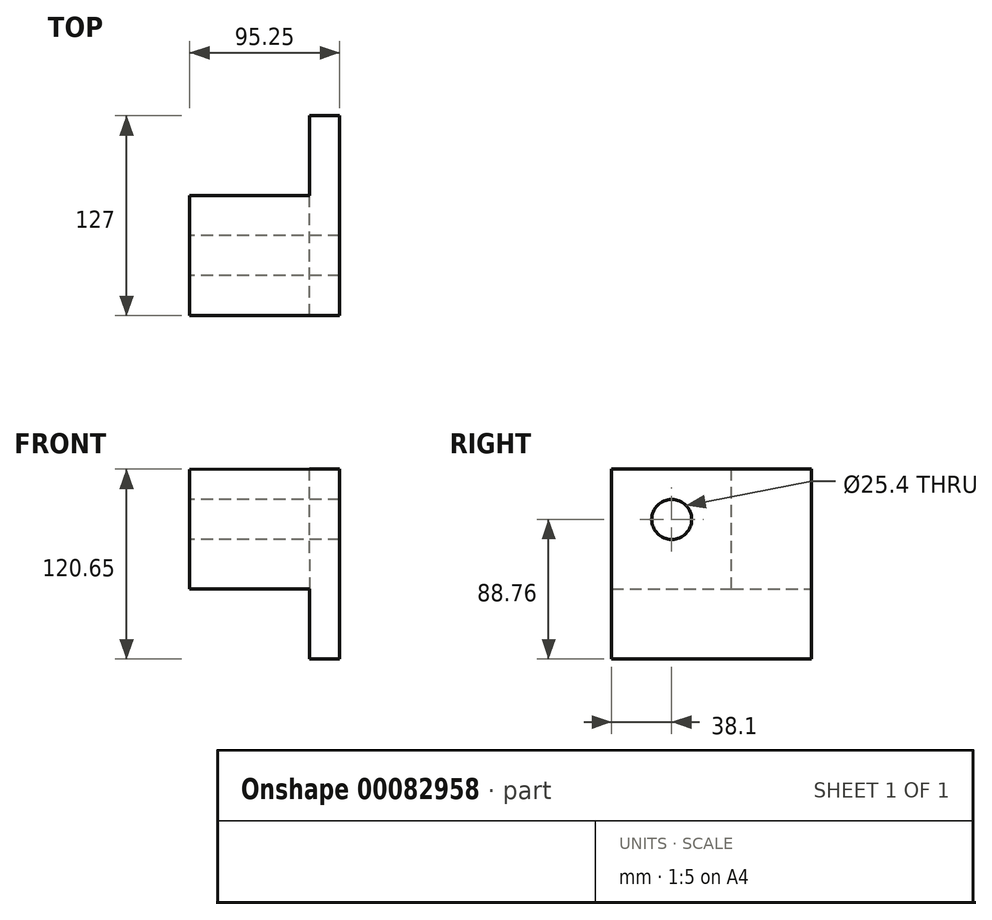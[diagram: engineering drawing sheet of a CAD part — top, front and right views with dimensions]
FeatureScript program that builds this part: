
annotation { "Feature Type Name" : "Feature", "Feature Type Description" : "" }
export const myFeature = defineFeature(function(context is Context, id is Id, definition is map)
    precondition{}
    {
        {
            var Q0;
            Q0=qCreatedBy(makeId("Front.planeOp"),FACE);
            var sketch = newSketch(context, id + "F0", { "sketchPlane" : qUnion([Q0])});
            skArc(sketch, "E0", {"start": v(0, 120.65) * mm, "mid": v(85.31, 85.31) * mm, "end": v(120.65, 0) * mm});
            skLineSegment(sketch, "E1", {"start": v(0, 120.65) * mm, "end": v(0, 0) * mm});
            skLineSegment(sketch, "E2", {"start": v(0, 0) * mm, "end": v(120.65, 0) * mm});
            skLineSegment(sketch, "E3.bottom", {"start": v(0, 120.65) * mm, "end": v(-19.05, 120.65) * mm});
            skLineSegment(sketch, "E3.top", {"start": v(0, 0) * mm, "end": v(-19.05, 0) * mm});
            skLineSegment(sketch, "E4", {"start": v(120.65, 0) * mm, "end": v(-95.25, 0) * mm});
            skLineSegment(sketch, "E5", {"start": v(-95.25, 0) * mm, "end": v(-95.25, 120.51) * mm});
            skLineSegment(sketch, "E6", {"start": v(-95.25, 120.51) * mm, "end": v(-19.05, 120.65) * mm});
            skSolve(sketch);
        }
        {
            var Q0;
            Q0=makeQuery(id+"F0.imprint","IMPRINT",FACE,{"disambiguationData":[TD([[makeQuery(id+"F0.imprint","IMPRINT",EDGE,{"derivedFrom":sQuery(id+"F0.wireOp",EDGE,"E3.bottom")}),1.0]])]});
            var Q1;
            {var subQ0=sQuery(id+"F0.wireOp",EDGE,"E0");Q1=makeQuery(id+"F0.imprint","IMPRINT",FACE,{"disambiguationData":[TD([[makeQuery(id+"F0.imprint","IMPRINT",EDGE,{"derivedFrom":subQ0}),-1.0]])]});}
            extrude(context, id + "F1", {"entities" : qUnion([Q0, Q1]), "depth" : 127 * mm});
        }
        {
            var Q0;
            Q0=makeQuery(id+"F1.opExtrude","SWEPT_FACE",FACE,{"disambiguationData":[OSD([sQuery(id+"F0.wireOp",EDGE,"E5")])]});
            var sketch = newSketch(context, id + "F2", { "sketchPlane" : qUnion([Q0])});
            skLineSegment(sketch, "E7", {"start": v(127, 120.51) * mm, "end": v(50.8, 120.51) * mm});
            skLineSegment(sketch, "E8", {"start": v(127, 0) * mm, "end": v(127, 44.45) * mm});
            skLineSegment(sketch, "E9", {"start": v(127, 44.45) * mm, "end": v(127, 120.51) * mm});
            skLineSegment(sketch, "E10", {"start": v(127, 44.45) * mm, "end": v(50.8, 44.45) * mm});
            skLineSegment(sketch, "E11", {"start": v(50.8, 44.45) * mm, "end": v(50.8, 120.51) * mm});
            skSolve(sketch);
        }
        {
            var Q0;
            Q0=makeQuery(id+"F2.imprint","IMPRINT",FACE,{"disambiguationData":[TD([[makeQuery(id+"F2.imprint","IMPRINT",EDGE,{"derivedFrom":sQuery(id+"F2.wireOp",EDGE,"E8")}),1.0]])]});
            extrude(context, id + "F3", {"entities" : qUnion([Q0]), "operationType" : NewBodyOperationType.REMOVE, "oppositeDirection" : true, "depth" : 76.2 * mm});
        }
        {
            var Q0;
            Q0=makeQuery(id+"F1.opExtrude","SWEPT_FACE",FACE,{"disambiguationData":[OSD([sQuery(id+"F0.wireOp",EDGE,"E6")])]});
            var sketch = newSketch(context, id + "F4", { "sketchPlane" : qUnion([Q0])});
            skLineSegment(sketch, "E12", {"start": v(-95.03, -50.8) * mm, "end": v(-18.83, -50.8) * mm});
            skLineSegment(sketch, "E13", {"start": v(-18.83, -50.8) * mm, "end": v(-18.83, 0) * mm});
            skLineSegment(sketch, "E14", {"start": v(-18.83, 0) * mm, "end": v(-95.03, 0) * mm});
            skLineSegment(sketch, "E15", {"start": v(-95.03, 0) * mm, "end": v(-95.03, -50.8) * mm});
            skSolve(sketch);
        }
        {
            var Q0;
            Q0=makeQuery(id+"F4.imprint","IMPRINT",FACE,{"disambiguationData":[TD([[makeQuery(id+"F4.imprint","IMPRINT",EDGE,{"derivedFrom":sQuery(id+"F4.wireOp",EDGE,"E12")}),1.0]])]});
            extrude(context, id + "F5", {"entities" : qUnion([Q0]), "operationType" : NewBodyOperationType.REMOVE, "oppositeDirection" : true, "depth" : 76.2 * mm});
        }
        {
            var Q0;
            Q0=makeQuery(id+"F1.opExtrude","SWEPT_FACE",FACE,{"disambiguationData":[OSD([sQuery(id+"F0.wireOp",EDGE,"E5")])]});
            var sketch = newSketch(context, id + "F6", { "sketchPlane" : qUnion([Q0])});
            skLineSegment(sketch, "E16", {"start": v(127, 120.51) * mm, "end": v(88.9, 120.51) * mm});
            skLineSegment(sketch, "E17", {"start": v(88.9, 120.51) * mm, "end": v(88.9, 88.76) * mm});
            skCircle(sketch, "E18", {"center": v(88.9, 88.76) * mm, "radius": 12.7 * mm});
            skSolve(sketch);
        }
        {
            var Q0;
            Q0=sQuery(id+"F6.wireOp",VERTEX,"E18.center");
            var Q1;
            Q1=makeQuery(id+"F1.opExtrude","SWEPT_BODY",BODY,{"disambiguationData":[OSD([sQuery(id+"F0.wireOp",EDGE,"E0"),sQuery(id+"F0.wireOp",EDGE,"E3.bottom"),sQuery(id+"F0.wireOp",EDGE,"E4"),sQuery(id+"F0.wireOp",EDGE,"E5"),sQuery(id+"F0.wireOp",EDGE,"E6")])]});
            hole(context, id + "F7", {"style" : HoleStyle.SIMPLE, "endStyle" : HoleEndStyle.THROUGH, "holeDiameter" : 25.4 * mm, "locations" : qUnion([Q0]), "scope" : qUnion([Q1]), "isTappedThrough" : true});
        }
        {
            var Q0;
            Q0=makeQuery(id+"F1.opExtrude","CAP_FACE",FACE,{"disambiguationData":[OSD([sQuery(id+"F0.wireOp",EDGE,"E0"),sQuery(id+"F0.wireOp",EDGE,"E3.bottom"),sQuery(id+"F0.wireOp",EDGE,"E4"),sQuery(id+"F0.wireOp",EDGE,"E5"),sQuery(id+"F0.wireOp",EDGE,"E6")])],"isStart":false});
            var sketch = newSketch(context, id + "F8", { "sketchPlane" : qUnion([Q0])});
            skLineSegment(sketch, "E19", {"start": v(120.65, 0) * mm, "end": v(57.15, 0) * mm});
            skLineSegment(sketch, "E20", {"start": v(57.15, 0) * mm, "end": v(57.15, 44.45) * mm});
            skCircle(sketch, "E21", {"center": v(57.15, 44.45) * mm, "radius": 12.7 * mm});
            skSolve(sketch);
        }
        {
            var Q0;
            Q0=sQuery(id+"F8.wireOp",VERTEX,"E20.end");
            var Q1;
            Q1=makeQuery(id+"F1.opExtrude","SWEPT_BODY",BODY,{"disambiguationData":[OSD([sQuery(id+"F0.wireOp",EDGE,"E0"),sQuery(id+"F0.wireOp",EDGE,"E3.bottom"),sQuery(id+"F0.wireOp",EDGE,"E4"),sQuery(id+"F0.wireOp",EDGE,"E5"),sQuery(id+"F0.wireOp",EDGE,"E6")])]});
            hole(context, id + "F9", {"style" : HoleStyle.SIMPLE, "endStyle" : HoleEndStyle.THROUGH, "holeDiameter" : 25.4 * mm, "locations" : qUnion([Q0]), "scope" : qUnion([Q1]), "isTappedThrough" : true});
        }
    });
